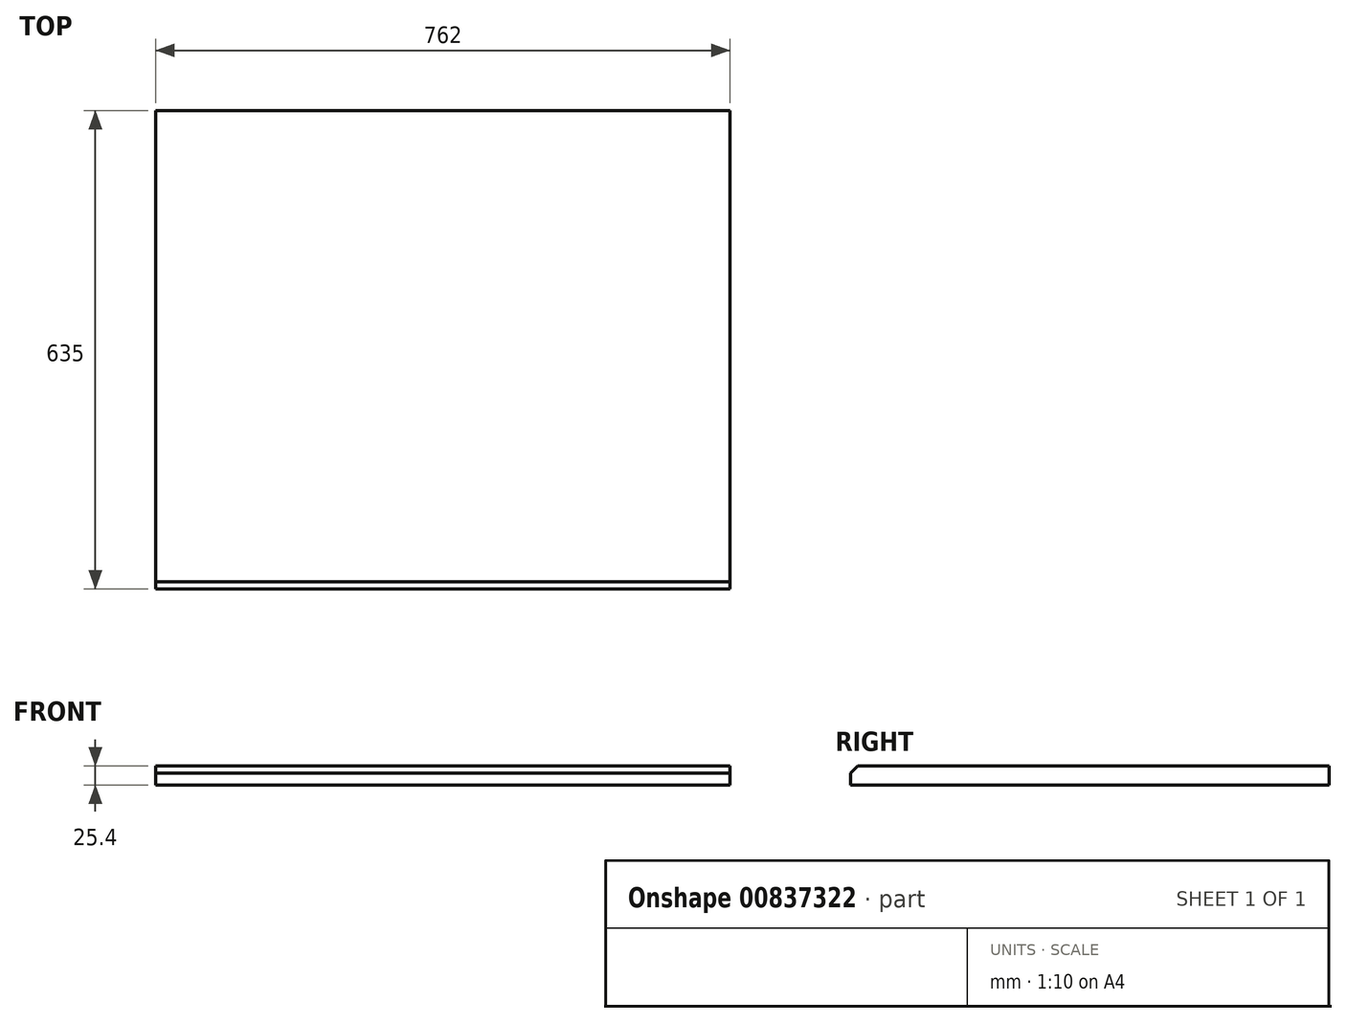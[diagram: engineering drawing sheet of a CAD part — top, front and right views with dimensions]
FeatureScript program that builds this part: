
annotation { "Feature Type Name" : "Feature", "Feature Type Description" : "" }
export const myFeature = defineFeature(function(context is Context, id is Id, definition is map)
    precondition{}
    {
        {
            var Q0;
            Q0=qCreatedBy(makeId("Right.planeOp"),FACE);
            var sketch = newSketch(context, id + "F0", { "sketchPlane" : qUnion([Q0])});
            skLineSegment(sketch, "E0.bottom", {"start": v(0, 0) * mm, "end": v(-635, 0) * mm});
            skLineSegment(sketch, "E0.top", {"start": v(0, -25.4) * mm, "end": v(-635, -25.4) * mm});
            skLineSegment(sketch, "E0.left", {"start": v(0, 0) * mm, "end": v(0, -25.4) * mm});
            skLineSegment(sketch, "E0.right", {"start": v(-635, 0) * mm, "end": v(-635, -25.4) * mm});
            skSolve(sketch);
        }
        {
            var Q0;
            Q0=makeQuery(id+"F0.imprint","IMPRINT",FACE,{"disambiguationData":[TD([[makeQuery(id+"F0.imprint","IMPRINT",EDGE,{"derivedFrom":sQuery(id+"F0.wireOp",EDGE,"E0.bottom")}),1.0]])]});
            extrude(context, id + "F1", {"entities" : qUnion([Q0]), "endBound" : BoundingType.SYMMETRIC, "depth" : 762 * mm, "offsetDistance" : 25.4 * mm});
        }
        {
            var Q0;
            Q0=makeQuery(id+"F1.opExtrude","SWEPT_EDGE",EDGE,{"disambiguationData":[OSD([sQuery(id+"F0.wireOp",EDGE,"E0.bottom"),sQuery(id+"F0.wireOp",EDGE,"E0.right")])]});
            chamfer(context, id + "F2", {"entities" : qUnion([Q0]), "width" : 9.52 * mm, "tangentPropagation" : true});
        }
    });
